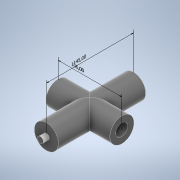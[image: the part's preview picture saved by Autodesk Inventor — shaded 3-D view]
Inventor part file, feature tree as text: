
AUTODESK INVENTOR PART (.ipt)
format: ipt  version: 2021 (Build 250183000, 183)  size: 147,456 bytes
history: native  units: mm
features: extrude x6, sketch x6, other x3
ambient origin geometry x8: Origin, YZ Plane, XZ Plane, XY Plane, X Axis, Y Axis, Z Axis, Center Point
bodies: Solid1 (feature_tree)
feature tree (15):
  other  "Annotations"
  extrude  "Extrusion1"  Depth=106.0mm TaperAngle=0.0deg
  extrude  "Extrusion2"  Depth=10.0mm TaperAngle=0.0deg
  extrude  "Extrusion3"  Depth=10.0mm TaperAngle=0.0deg
  extrude  "Extrusion4"  Depth=10.0mm
  extrude  "Extrusion5"  Depth=10.0mm TaperAngle=0.0deg
  extrude  "Extrusion6"  [1 undecoded]
  sketch  "Sketch1"  dims[d0=40.0mm d1=106.0mm d2=0.0mm]
  sketch  "Sketch2"  dims[d3=20.0mm d4=10.0mm d5=0.0mm]
  sketch  "Sketch3"  dims[d6=20.0mm d7=10.0mm d8=0.0mm]
  sketch  "Sketch5"  dims[d10=145.0mm d11=0.0mm d12=10.0mm]
  sketch  "Sketch6"  dims[d13=10.0mm d14=0.0mm d15=10.0mm d16=0.0mm]
  sketch  "Sketch7"  dims[d17=145.0mm d18=106.0mm]
  other  "Linear Dimension 1"
  other  "Linear Dimension 2"
note: 1 required parameter value undecoded (feature->parameter linkage not recoverable at this tier; creation-order binding heuristic only, values carry confidence <= 0.55)
